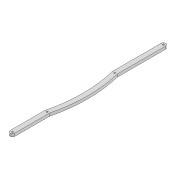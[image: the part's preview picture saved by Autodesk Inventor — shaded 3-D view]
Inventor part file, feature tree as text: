
AUTODESK INVENTOR PART (.ipt)
format: ipt  version: 2022 (Build 260153000, 153)  size: 102,912 bytes
history: native  units: mm
features: extrude x1, other x1, sketch x1
ambient origin geometry x8: Origin, YZ Plane, XZ Plane, XY Plane, X Axis, Y Axis, Z Axis, Center Point
bodies: Solid1 (feature_tree)
feature tree (3):
  extrude  "Extrusion1"  Depth=300.0mm
  other  "Work Axis3"
  sketch  "Sketch1"  dims[d0=3.3mm d1=3.3mm d2=10.0mm d3=322.934mm d4=3.3mm d5=74.182mm d6=6.0mm d7=0.0mm d8=3.3mm d9=218.733mm d10=300.0mm d11=300.0mm]
